# Revit family: IS_Mia_J4697_BIM_DE
name_source: partatom
category: Plumbing Fixtures
revit_build: Autodesk Revit MEP 2016 (Build: 20161004_0715(x64)
units: mm (PartAtom-declared; Revit-internal decimal feet)

## family parameters
Always vertical = No
Cut with Voids When Loaded = No
OmniClass Number = 23.45.05.21.11
OmniClass Title = Water Closets
Part Type = Normal
Room Calculation Point = No
Round Connector Dimension = Use Diameter
Shared = No
Work Plane-Based = No

## types (1)
- J469701 MIA seat & cover, slow close
    Accessories = www.idealstandard.de\ersatzteile
    AssetType = Fixed
    BIMObjectName = ISI_IdealStandard_WcSeatsAndCovers_Mia_J469701
    BOSUseNativeGeometries = 1
    BarCode = 8023246238121
    Brand = Ideal Standard
    Brand url = http://www.idealstandard.de
    Color = White
    ConnectionType = Plumbing
    Cost = 0 $
    CurrencyUnit = €
    CurrentRevision = 1
    Date of publishing = 20/12/2017
    Description = IS WC-Sitz MIA, Softclosing, Weiß
    DurationUnit = Year
    EAN code = https://8023246238121
    Edition number = 1
    ExpectedLife = 25
    Features = IS WC-Sitz MIA, Softclosing, Weiß
    Finish = White
    IFC Classification = Sanitary Terminal
    IfcExportAs = IfcSanitaryTerminalType
    Installation instructions = http://www.idealstandard.de
    InstallationInstructions = www.idealstandard.de\produkte
    MainColor = White
    MaintenanceInformation = www.idealstandard.de\produkte
    Manufacturer name = Ideal Standard
    ManufacturerURL = http://www.idealstandard.de
    Material = Duroplast
    Model = J469701
    ModelNumber = J469701
    ModelReference = IS WC-Sitz MIA, Softclosing, Weiß
    Name = WcSeatsAndCovers_Mia_J469701
    NettWeight = 2 Kg
    Nominal height = 55
    Nominal width = 450
    NominalDepth = 452 mm  [stored 1.48294 ft]
    NominalHeight = 58 mm
    NominalLength = 452 mm  [stored 1.48294 ft]
    NominalWidth = 360 mm
    OutletConnectionSize = 0 mm  [stored 0 ft]
    Product Guid = 1db86b75-897a-49ae-9e3a-297b660d6e46
    Product SKU = J4697
    Product data url = https://bimobject.com
    Product family = Sanitary
    Product group = Seat & Cover
    Product name = MIA seat & cover, slow close
    Product url = http://www.idealstandard.de
    ProductInformation = www.idealstandard.de/produkte
    QR code = http://bimobject.com
    Shape = Sculptured
    Size = 360x452x58 mm
    Space = Internal
    SpareParts = www.idealstandard.de/ersatzteile
    SpilloverLevel = 0 mm  [stored 0 ft]
    Technical description = http://www.idealstandard.de
    URL = http://www.idealstandard.de
    Uniclass2015Code = Pr_40_20_93_95
    Uniclass2015Title = WC seats and covers
    Uniclass2015Version = Products v1.1
    Version = 1
    VolumeUnits = Litres
    Weight Net (Kg) = 2

note: [stored X ft] marks values corroborated as IEEE doubles in the binary element streams (Revit-internal decimal feet)

## geometry (parser evidence)
native form markers: Blend x4
no freeform markers — native parametric forms only
